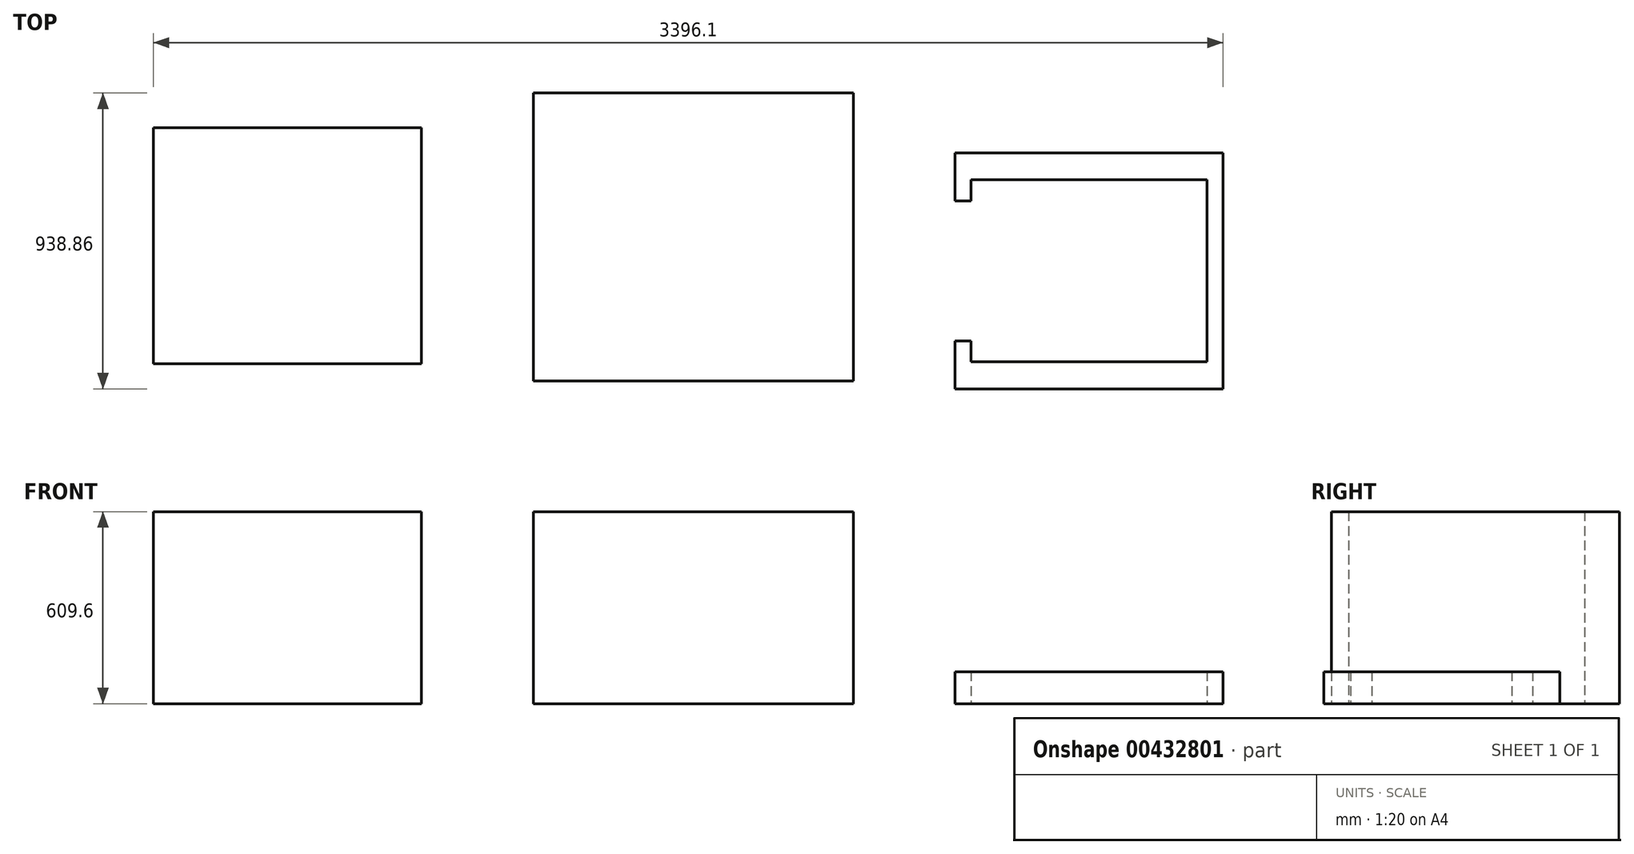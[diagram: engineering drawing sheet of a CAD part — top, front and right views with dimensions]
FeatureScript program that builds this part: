
annotation { "Feature Type Name" : "Feature", "Feature Type Description" : "" }
export const myFeature = defineFeature(function(context is Context, id is Id, definition is map)
    precondition{}
    {
        {
            var Q0;
            Q0=qCreatedBy(makeId("Top.planeOp"),FACE);
            var sketch = newSketch(context, id + "F0", { "sketchPlane" : qUnion([Q0])});
            skLineSegment(sketch, "E0.bottom", {"start": v(-572.13, 395.88) * mm, "end": v(443.87, 395.88) * mm});
            skLineSegment(sketch, "E0.top", {"start": v(-572.13, -518.52) * mm, "end": v(443.87, -518.52) * mm});
            skLineSegment(sketch, "E0.left", {"start": v(-572.13, 395.88) * mm, "end": v(-572.13, -518.52) * mm});
            skLineSegment(sketch, "E0.right", {"start": v(443.87, 395.88) * mm, "end": v(443.87, -518.52) * mm});
            skSolve(sketch);
        }
        {
            var Q0;
            Q0=qSketchRegion(id+"F0",true);
            extrude(context, id + "F1", {"entities" : qUnion([Q0]), "depth" : 609.6 * mm});
        }
        {
            var Q0;
            Q0=qCreatedBy(makeId("Top.planeOp"),FACE);
            var sketch = newSketch(context, id + "F2", { "sketchPlane" : qUnion([Q0])});
            skLineSegment(sketch, "E1.bottom", {"start": v(-1779.38, 285.49) * mm, "end": v(-928.48, 285.49) * mm});
            skLineSegment(sketch, "E1.top", {"start": v(-1779.38, -463.81) * mm, "end": v(-928.48, -463.81) * mm});
            skLineSegment(sketch, "E1.left", {"start": v(-1779.38, 285.49) * mm, "end": v(-1779.38, -463.81) * mm});
            skLineSegment(sketch, "E1.right", {"start": v(-928.48, 285.49) * mm, "end": v(-928.48, -463.81) * mm});
            skSolve(sketch);
        }
        {
            var Q0;
            Q0=makeQuery(id+"F2.imprint","IMPRINT",FACE,{"disambiguationData":[TD([[makeQuery(id+"F2.imprint","IMPRINT",EDGE,{"derivedFrom":sQuery(id+"F2.wireOp",EDGE,"E1.bottom")}),-1.0]])]});
            extrude(context, id + "F3", {"entities" : qUnion([Q0]), "operationType" : NewBodyOperationType.ADD, "depth" : 609.6 * mm});
        }
        {
            var Q0;
            Q0=qCreatedBy(makeId("Top.planeOp"),FACE);
            var sketch = newSketch(context, id + "F4", { "sketchPlane" : qUnion([Q0])});
            skLineSegment(sketch, "E2.bottom", {"start": v(765.82, 206.32) * mm, "end": v(1616.72, 206.32) * mm});
            skLineSegment(sketch, "E2.top", {"start": v(765.82, -542.98) * mm, "end": v(1616.72, -542.98) * mm});
            skLineSegment(sketch, "E2.left", {"start": v(765.82, 206.32) * mm, "end": v(765.82, 53.92) * mm});
            skLineSegment(sketch, "E2.right", {"start": v(1616.72, 206.32) * mm, "end": v(1616.72, -542.98) * mm});
            skLineSegment(sketch, "E3.bottom", {"start": v(816.62, -457.26) * mm, "end": v(1565.92, -457.26) * mm});
            skLineSegment(sketch, "E3.top", {"start": v(816.62, 120.6) * mm, "end": v(1565.92, 120.6) * mm});
            skLineSegment(sketch, "E3.left", {"start": v(816.62, -457.26) * mm, "end": v(816.62, -390.58) * mm});
            skLineSegment(sketch, "E3.right", {"start": v(1565.92, -457.26) * mm, "end": v(1565.92, 120.6) * mm});
            skLineSegment(sketch, "E4", {"start": v(765.82, -390.58) * mm, "end": v(816.62, -390.58) * mm});
            skLineSegment(sketch, "E5", {"start": v(765.82, 53.92) * mm, "end": v(816.62, 53.92) * mm});
            skLineSegment(sketch, "E6.trimOffspring", {"start": v(816.62, 53.92) * mm, "end": v(816.62, 120.6) * mm});
            skLineSegment(sketch, "E7.trimOffspring", {"start": v(765.82, -390.58) * mm, "end": v(765.82, -542.98) * mm});
            skSolve(sketch);
        }
        {
            var Q0;
            Q0=makeQuery(id+"F4.imprint","IMPRINT",FACE,{"disambiguationData":[TD([[makeQuery(id+"F4.imprint","IMPRINT",EDGE,{"derivedFrom":sQuery(id+"F4.wireOp",EDGE,"E2.bottom")}),-1.0]])]});
            extrude(context, id + "F5", {"entities" : qUnion([Q0]), "depth" : 101.6 * mm});
        }
    });
